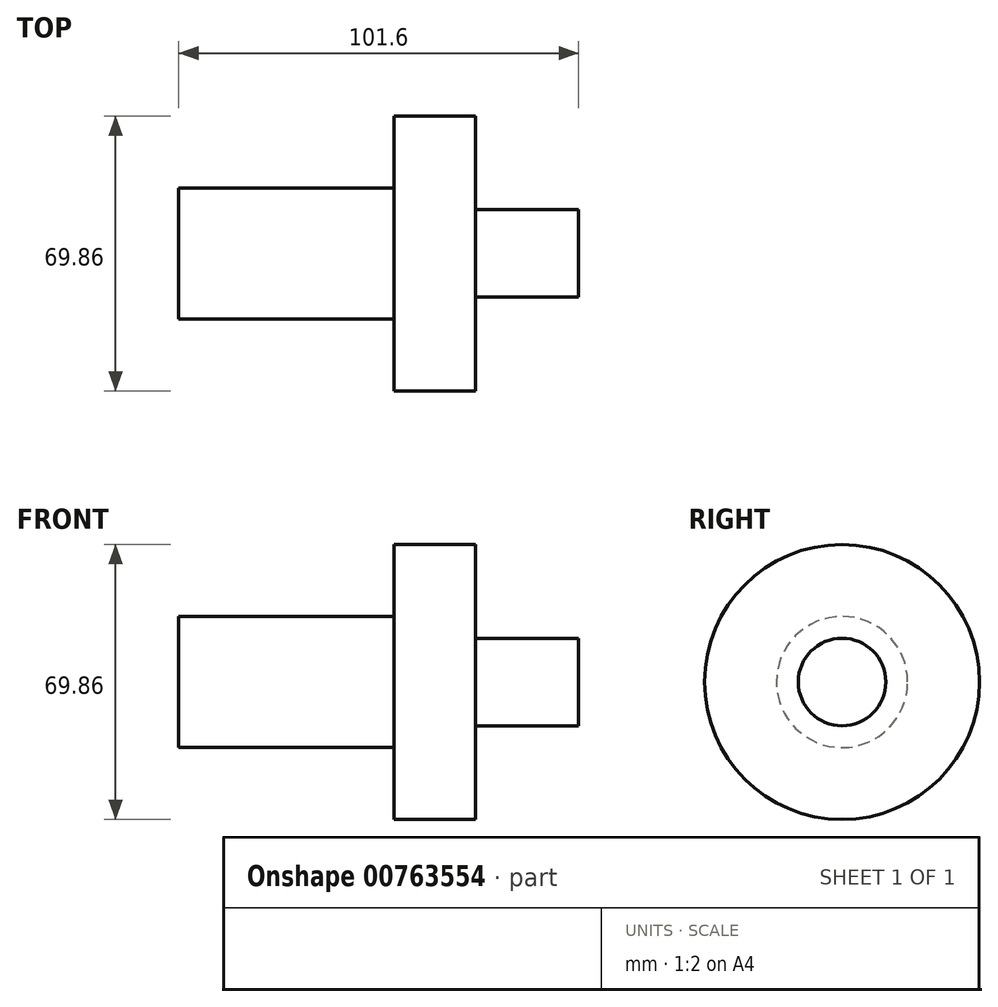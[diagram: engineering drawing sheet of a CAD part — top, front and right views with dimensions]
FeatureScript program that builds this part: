
annotation { "Feature Type Name" : "Feature", "Feature Type Description" : "" }
export const myFeature = defineFeature(function(context is Context, id is Id, definition is map)
    precondition{}
    {
        {
            var Q0;
            Q0=qCreatedBy(makeId("Front.planeOp"),FACE);
            var sketch = newSketch(context, id + "F0", { "sketchPlane" : qUnion([Q0])});
            skLineSegment(sketch, "E0", {"start": v(-65.76, 0) * mm, "end": v(83.68, 0) * mm, "construction": true});
            skLineSegment(sketch, "E1", {"start": v(0, 63.12) * mm, "end": v(0, -67.19) * mm, "construction": true});
            skLineSegment(sketch, "E2", {"start": v(-54.77, 0) * mm, "end": v(-54.77, 16.67) * mm});
            skLineSegment(sketch, "E3", {"start": v(-54.77, 16.67) * mm, "end": v(0, 16.67) * mm});
            skLineSegment(sketch, "E4", {"start": v(0, 16.67) * mm, "end": v(0, 34.93) * mm});
            skLineSegment(sketch, "E5", {"start": v(0, 34.93) * mm, "end": v(20.64, 34.93) * mm});
            skLineSegment(sketch, "E6", {"start": v(20.64, 34.93) * mm, "end": v(20.64, 11.11) * mm});
            skLineSegment(sketch, "E7", {"start": v(20.64, 11.11) * mm, "end": v(46.83, 11.11) * mm});
            skLineSegment(sketch, "E8", {"start": v(46.83, 11.11) * mm, "end": v(46.83, 0) * mm});
            skLineSegment(sketch, "E9", {"start": v(-54.77, 0) * mm, "end": v(46.83, 0) * mm});
            skSolve(sketch);
        }
        {
            var Q0;
            Q0=makeQuery(id+"F0.imprint","IMPRINT",FACE,{"disambiguationData":[TD([[makeQuery(id+"F0.imprint","IMPRINT",EDGE,{"derivedFrom":sQuery(id+"F0.wireOp",EDGE,"E2")}),-1.0]])]});
            var Q1;
            Q1=sQuery(id+"F0.wireOp",EDGE,"E9");
            revolve(context, id + "F1", {"surfaceOperationType" : NewSurfaceOperationType.NEW, "entities" : qUnion([Q0]), "axis" : qUnion([Q1]), "revolveType" : RevolveType.FULL});
        }
    });
